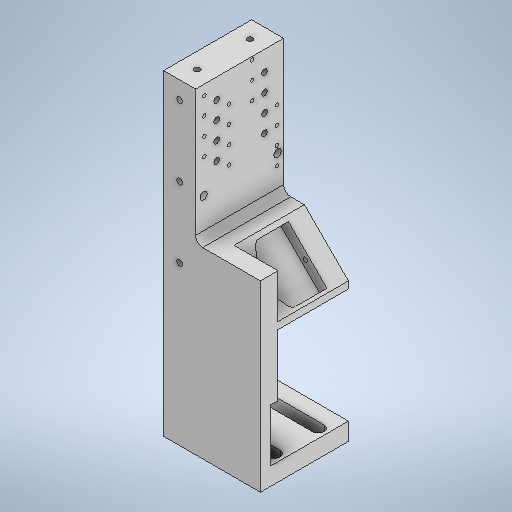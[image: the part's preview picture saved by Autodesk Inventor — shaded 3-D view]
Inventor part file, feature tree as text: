
AUTODESK INVENTOR PART (.ipt)
format: ipt  version: 2025 (Build 290162010, 162A)  size: 603,136 bytes
history: native  units: in
note: dims shown in document units (in); Inventor stores cm internally (conversion verified against a paired STEP export)
features: sketch x26, extrude x16, hole x10, fillet x3
ambient origin geometry x8: Origin, YZ Plane, XZ Plane, XY Plane, X Axis, Y Axis, Z Axis, Center Point
bodies: Solid1 (feature_tree)
feature tree (55):
  extrude  "Extrusion1"  Depth=2.9528in
  extrude  "Extrusion2"  Depth=0.3937in
  extrude  "Extrusion3"  Depth=0.3937in
  extrude  "Extrusion5"  TaperAngle=0.0deg  [1 undecoded]
  hole  "Hole2"  [1 undecoded]
  extrude  "Extrusion6"  Depth=0.4694in
  hole  "Hole5"  [1 undecoded]
  extrude  "Extrusion10"  Depth=1.0709in
  extrude  "Extrusion11"  Depth=0.3937in
  extrude  "Extrusion12"  Depth=0.7874in
  sketch  "Sketch22"  dims[d119=3.2938in d120=0.0in d121=0.7874in]
  extrude  "Extrusion13"  TaperAngle=45.0deg  [1 undecoded]
  extrude  "Extrusion14"  Depth=1.5748in TaperAngle=0.0deg
  extrude  "Extrusion15"  Depth=0.6347in
  extrude  "Extrusion16"  Depth=0.2362in TaperAngle=0.0deg
  hole  "Hole8"  [1 undecoded]
  extrude  "Extrusion17"  Depth=0.2362in
  extrude  "Extrusion18"  Depth=0.6299in
  hole  "Hole9"  [1 undecoded]
  hole  "Hole10"  [1 undecoded]
  hole  "Hole12"  [1 undecoded]
  extrude  "Extrusion22"  Depth=0.3937in
  fillet  "Fillet2"  Radius=0.3937in
  hole  "Hole13"  [1 undecoded]
  hole  "Hole14"  [1 undecoded]
  hole  "Hole15"  [1 undecoded]
  hole  "Hole16"  [1 undecoded]
  extrude  "Extrusion24"  Depth=0.1575in
  fillet  "Fillet3"  Radius=0.3504in
  fillet  "Fillet5"  Radius=0.3504in
  sketch  "Sketch1"  dims[d0=2.9528in d1=2.9528in]
  sketch  "Sketch2"  dims[d2=0.3937in d3=0.0in d4=0.3937in]
  sketch  "Sketch3"  dims[d5=3.937in d6=0.0in d7=0.3937in]
  sketch  "Sketch8"  dims[d8=7.874in d9=0.0in d26=0.0in]
  sketch  "Sketch9"  dims[d27=2.7559in d28=0.3228in d29=0.3937in d30=0.0in d31=0.0in]
  sketch  "Sketch10"  dims[d32=5.4615in d33=0.4694in]
  sketch  "Sketch12"  dims[d34=0.1276in d35=0.315in d36=0.1575in d37=0.0787in d38=90.0deg d39=0.4646in d40=0.8108in d41=0.5906in]
  sketch  "Sketch18"  dims[d42=3.0477in d43=0.0in d62=1.0709in]
  sketch  "Sketch19"  dims[d65=1.0709in]
  sketch  "Sketch20"  dims[d66=0.1276in d67=0.315in d68=0.1575in d69=0.0787in d70=90.0deg d71=0.4646in d72=0.8108in d118=0.3937in]
  sketch  "Sketch23"  dims[d122=2.1147in d123=0.0in d124=45.0deg]
  sketch  "Sketch24"  dims[d125=3.1102in d126=1.5748in d127=0.0in]
  sketch  "Sketch27"  dims[d129=1.0in d130=0.6347in]
  sketch  "Sketch28"  dims[d131=0.1575in d132=0.0in d133=0.2362in d134=0.0in]
  sketch  "Sketch29"  dims[d135=1.8888in d136=0.0in d138=0.9843in]
  sketch  "Sketch30"  dims[d139=0.2362in d140=0.0in d142=0.1181in]
  sketch  "Sketch31"  dims[d143=0.5323in]
  sketch  "Sketch32"  dims[d144=0.0968in d145=0.5118in d146=0.4724in d147=0.1724in d148=90.0deg d149=0.5118in d150=0.8108in d151=0.6299in]
  sketch  "Sketch33"  dims[d152=0.748in d153=0.7874in]
  sketch  "Sketch38"  dims[d154=1.2205in d155=0.2362in d156=0.0in]
  sketch  "Sketch40"  dims[d157=0.0in d158=0.0in d160=0.3937in]
  sketch  "Sketch41"  dims[d161=0.3937in d162=0.3937in d163=0.3937in]
  sketch  "Sketch42"  dims[d164=1.0709in d165=1.0709in]
  sketch  "Sketch43"  dims[d166=0.3937in d167=0.3937in]
  sketch  "Sketch44"  dims[d168=1.0709in d169=0.1276in d170=0.315in d171=0.1575in d172=0.0787in d173=90.0deg d174=0.4646in d175=0.8108in d176=-0.3092in d177=0.3504in d178=0.3504in d179=0.3504in d180=0.3504in d181=0.3504in d182=0.3504in d183=0.3504in d184=0.3504in d185=0.2756in d186=0.2756in d187=0.0787in d188=0.328in d189=0.1575in d190=0.0787in d191=90.0deg d192=0.1969in d193=0.0in d194=-0.3092in d195=0.3504in d196=0.3504in d197=0.3504in d198=0.3504in d199=0.3504in d200=0.3504in d201=0.3504in d202=0.3504in d203=0.2756in d204=0.2756in d212=0.0787in d213=0.2362in d214=0.1575in d215=0.0787in d216=90.0deg d217=0.1969in d218=0.0in d236=1.0in d237=0.4921in d238=0.1299in d239=1.2205in d240=0.1969in d241=1.2205in d242=0.1969in d243=0.1299in d244=0.4921in d245=0.0in d246=0.0in d251=0.1575in d252=4.5371in d253=0.1772in d254=0.2922in d255=0.1654in d256=0.315in d257=0.4961in d258=0.0787in d259=90.0deg d260=0.315in d261=0.0in d262=0.3583in d263=0.3583in d264=0.3583in d265=3.5433in d266=1.5748in d267=1.5748in d268=0.1276in d269=0.1969in d270=0.3701in d271=0.0787in d272=90.0deg d273=0.3071in d274=0.0in d275=0.3583in d276=0.3583in d277=0.3583in d278=3.5433in d279=1.5748in d280=1.5748in d281=0.1276in d282=0.1969in d283=0.1575in d284=0.0787in d285=90.0deg d286=0.3071in d287=0.0in d288=0.3583in d289=0.3583in d290=0.3937in d291=0.3937in d292=1.1811in d293=0.1276in d294=0.1969in d295=0.1575in d296=0.0787in d297=90.0deg d298=0.3071in d299=0.0in d300=0.4331in d301=1.1811in d302=0.1575in d303=1.7717in d304=0.0in d305=0.1575in d311=0.1575in d75=0.0197in d76=0.0344in d77=0.0197in d78=0.0344in d219=0.0in d220=0.0in d221=0.0in d222=0.0in d310=0.0in d312=0.0in d313=0.0in]
note: 12 required parameter values undecoded (feature->parameter linkage not recoverable at this tier; creation-order binding heuristic only, values carry confidence <= 0.55)
